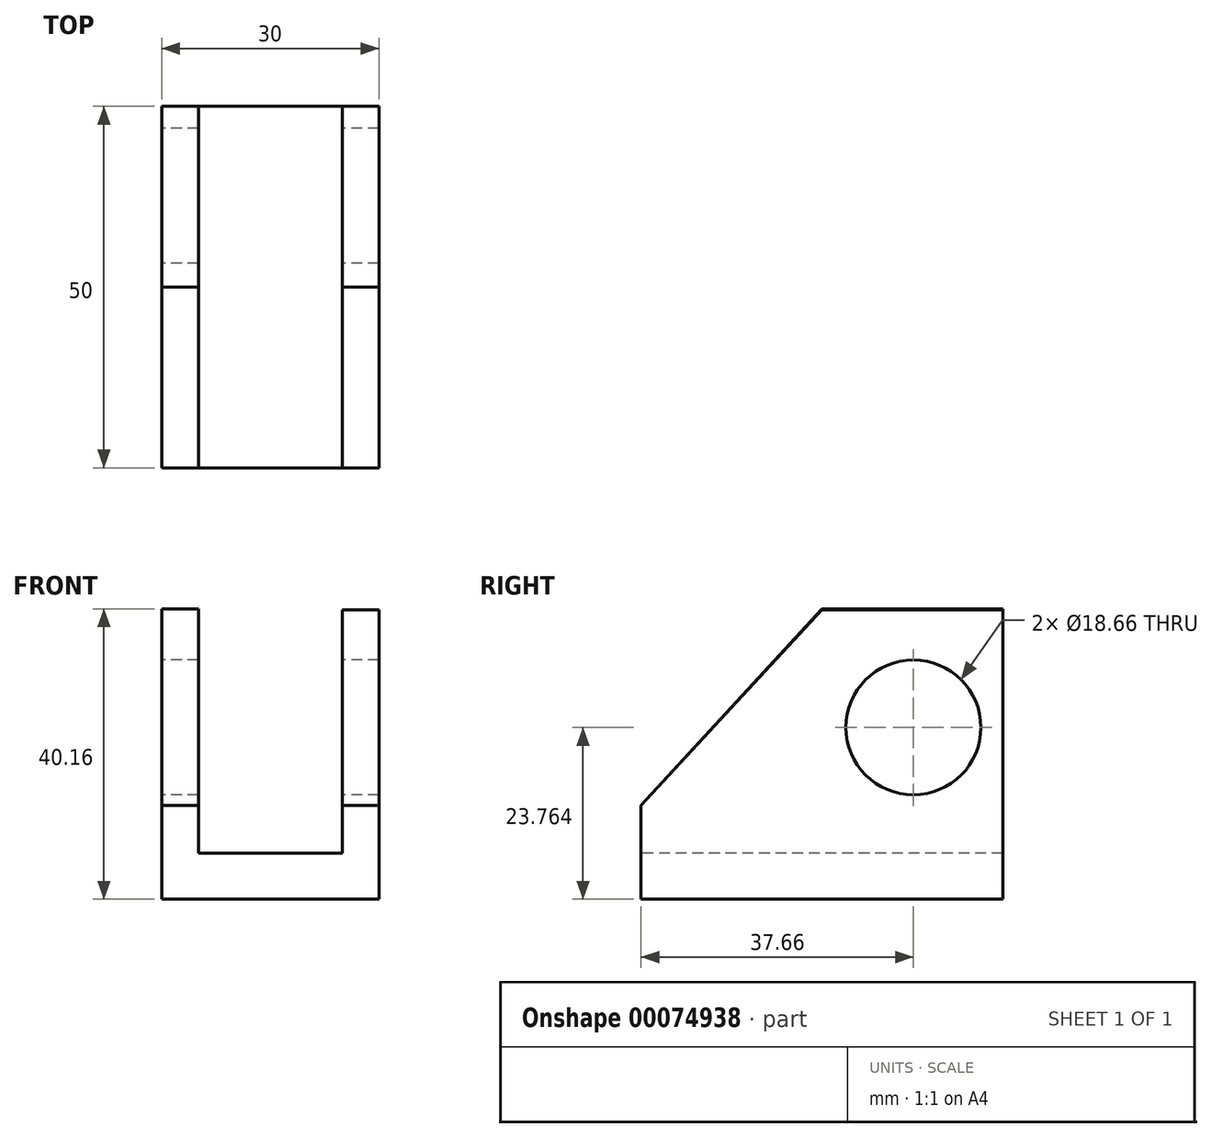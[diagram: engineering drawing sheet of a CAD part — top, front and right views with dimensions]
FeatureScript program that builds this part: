
annotation { "Feature Type Name" : "Feature", "Feature Type Description" : "" }
export const myFeature = defineFeature(function(context is Context, id is Id, definition is map)
    precondition{}
    {
        {
            var Q0;
            Q0=qCreatedBy(makeId("Front.planeOp"),FACE);
            var sketch = newSketch(context, id + "F0", { "sketchPlane" : qUnion([Q0])});
            skLineSegment(sketch, "E0.bottom", {"start": v(0, 0) * mm, "end": v(15, 0) * mm});
            skLineSegment(sketch, "E0.top", {"start": v(0, 6.35) * mm, "end": v(9.92, 6.35) * mm});
            skLineSegment(sketch, "E0.right", {"start": v(15, 0) * mm, "end": v(15, 6.35) * mm});
            skLineSegment(sketch, "E1.top", {"start": v(15, 12.95) * mm, "end": v(9.92, 12.95) * mm});
            skLineSegment(sketch, "E1.left", {"start": v(15, 6.35) * mm, "end": v(15, 12.95) * mm});
            skLineSegment(sketch, "E1.right", {"start": v(9.92, 6.35) * mm, "end": v(9.92, 12.95) * mm});
            skLineSegment(sketch, "E2.MirrorCS", {"start": v(0, 6.35) * mm, "end": v(-9.92, 6.35) * mm});
            skLineSegment(sketch, "E3.MirrorCS", {"start": v(-9.92, 6.35) * mm, "end": v(-9.92, 12.95) * mm});
            skLineSegment(sketch, "E4.MirrorCS", {"start": v(-15, 12.95) * mm, "end": v(-9.92, 12.95) * mm});
            skLineSegment(sketch, "E5.MirrorCS", {"start": v(-15, 6.35) * mm, "end": v(-15, 12.95) * mm});
            skLineSegment(sketch, "E6.MirrorCS", {"start": v(-15, 0) * mm, "end": v(-15, 6.35) * mm});
            skLineSegment(sketch, "E7.MirrorCS", {"start": v(0, 0) * mm, "end": v(-15, 0) * mm});
            skPoint(sketch, "E8.orphan", {"position": v(-15, 6.35) * mm});
            skSolve(sketch);
        }
        {
            var Q0;
            Q0 = qSketchRegion(id + "F0", true);
            extrude(context, id + "F1", {"entities" : qUnion([Q0]), "endBound" : BoundingType.SYMMETRIC, "oppositeDirection" : true, "depth" : 50 * mm});
        }
        {
            var Q0;
            Q0=makeQuery(id+"F1.opExtrude","SWEPT_FACE",FACE,{"disambiguationData":[OSD([sQuery(id+"F0.wireOp",EDGE,"E0.right"),sQuery(id+"F0.wireOp",EDGE,"E1.left")])]});
            var sketch = newSketch(context, id + "F2", { "sketchPlane" : qUnion([Q0])});
            skLineSegment(sketch, "E9.top", {"start": v(25, 40) * mm, "end": v(0, 40) * mm});
            skLineSegment(sketch, "E9.left", {"start": v(25, 12.95) * mm, "end": v(25, 40) * mm});
            skLineSegment(sketch, "E10", {"start": v(0, 40) * mm, "end": v(-25, 12.95) * mm});
            skLineSegment(sketch, "E11", {"start": v(-25, 12.95) * mm, "end": v(25, 12.95) * mm});
            skSolve(sketch);
        }
        {
            var Q0;
            Q0 = qSketchRegion(id + "F2", true);
            extrude(context, id + "F3", {"entities" : qUnion([Q0]), "operationType" : NewBodyOperationType.ADD, "oppositeDirection" : true, "depth" : 5.08 * mm});
        }
        {
            var Q0;
            Q0=makeQuery(id+"F1.opExtrude","SWEPT_FACE",FACE,{"disambiguationData":[OSD([sQuery(id+"F0.wireOp",EDGE,"E5.MirrorCS"),sQuery(id+"F0.wireOp",EDGE,"E6.MirrorCS")])]});
            var sketch = newSketch(context, id + "F4", { "sketchPlane" : qUnion([Q0])});
            skLineSegment(sketch, "E12.bottom", {"start": v(-25, 12.95) * mm, "end": v(0, 12.95) * mm});
            skLineSegment(sketch, "E12.top", {"start": v(-25, 40.16) * mm, "end": v(0, 40.16) * mm});
            skLineSegment(sketch, "E12.left", {"start": v(-25, 12.95) * mm, "end": v(-25, 40.16) * mm});
            skLineSegment(sketch, "E13", {"start": v(0, 40.16) * mm, "end": v(25, 12.95) * mm});
            skLineSegment(sketch, "E14", {"start": v(25, 12.95) * mm, "end": v(0, 12.95) * mm});
            skSolve(sketch);
        }
        {
            var Q0;
            Q0 = qSketchRegion(id + "F4", true);
            extrude(context, id + "F5", {"entities" : qUnion([Q0]), "operationType" : NewBodyOperationType.ADD, "oppositeDirection" : true, "depth" : 5.08 * mm});
        }
        {
            var Q0;
            Q0=makeQuery(id+"F5.boolean.opBoolean","MERGE",FACE,{"derivedFrom":[makeQuery(id+"F1.opExtrude","SWEPT_FACE",FACE,{"disambiguationData":[OSD([sQuery(id+"F0.wireOp",EDGE,"E5.MirrorCS"),sQuery(id+"F0.wireOp",EDGE,"E6.MirrorCS")])]}),makeQuery(id+"F5.opExtrude","CAP_FACE",FACE,{"disambiguationData":[OSD([sQuery(id+"F4.wireOp",EDGE,"E12.bottom"),sQuery(id+"F4.wireOp",EDGE,"E12.top"),sQuery(id+"F4.wireOp",EDGE,"E12.left"),sQuery(id+"F4.wireOp",EDGE,"E13"),sQuery(id+"F4.wireOp",EDGE,"E14")])],"isStart":true})]});
            var sketch = newSketch(context, id + "F6", { "sketchPlane" : qUnion([Q0])});
            skCircle(sketch, "E15", {"center": v(-12.66, 23.76) * mm, "radius": 9.33 * mm});
            skSolve(sketch);
        }
        {
            var Q0;
            Q0 = qSketchRegion(id + "F6", true);
            extrude(context, id + "F7", {"entities" : qUnion([Q0]), "operationType" : NewBodyOperationType.REMOVE, "endBound" : BoundingType.THROUGH_ALL, "oppositeDirection" : true, "depth" : 25.4 * mm});
        }
    });
